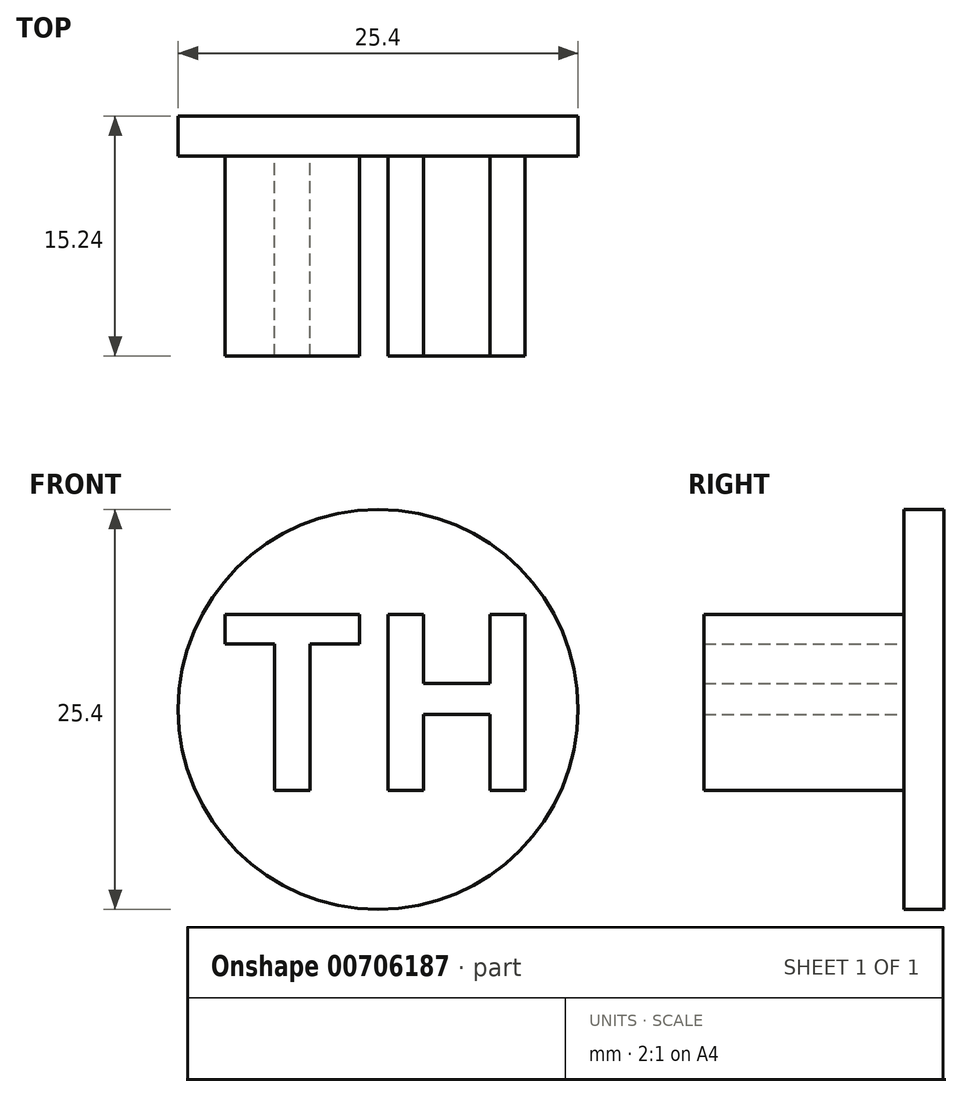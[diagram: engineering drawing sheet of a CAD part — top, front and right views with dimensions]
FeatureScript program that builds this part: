
annotation { "Feature Type Name" : "Feature", "Feature Type Description" : "" }
export const myFeature = defineFeature(function(context is Context, id is Id, definition is map)
    precondition{}
    {
        {
            var Q0;
            Q0=qCreatedBy(makeId("Front.planeOp"),FACE);
            var sketch = newSketch(context, id + "F0", { "sketchPlane" : qUnion([Q0])});
            skCircle(sketch, "E0", {"center": v(0, 0) * mm, "radius": 12.7 * mm});
            skSolve(sketch);
        }
        {
            var Q0;
            Q0=makeQuery(id+"F0.imprint","IMPRINT",FACE,{"disambiguationData":[TD([[makeQuery(id+"F0.imprint","IMPRINT",EDGE,{"derivedFrom":sQuery(id+"F0.wireOp",EDGE,"E0")}),1.0]])]});
            extrude(context, id + "F1", {"entities" : qUnion([Q0]), "depth" : 2.54 * mm, "offsetDistance" : 25.4 * mm});
        }
        {
            var Q0;
            Q0=makeQuery(id+"F1.opExtrude","CAP_FACE",FACE,{"disambiguationData":[OSD([sQuery(id+"F0.wireOp",EDGE,"E0")])],"isStart":false});
            var sketch = newSketch(context, id + "F2", { "sketchPlane" : qUnion([Q0])});
            skText(sketch, "E1", { "text": "TH ", "fontName": "NotoSansCJKtc-Bold.otf"});
            const initialGuessF2  = {"E1": [-0.01016, -0.00513, 1, 0, 0.01086]};
            skSetInitialGuess(sketch, initialGuessF2);
            skSolve(sketch);
        }
        {
            var Q0;
            Q0=makeQuery(id+"F2.imprint","IMPRINT",FACE,{"disambiguationData":[TD([[makeQuery(id+"F2.imprint","IMPRINT",EDGE,{"derivedFrom":sQuery(id+"F2.wireOp",EDGE,"E1.sketch_text.stroke-0")}),1.0]])]});
            var Q1;
            Q1=makeQuery(id+"F2.imprint","IMPRINT",FACE,{"disambiguationData":[TD([[makeQuery(id+"F2.imprint","IMPRINT",EDGE,{"derivedFrom":sQuery(id+"F2.wireOp",EDGE,"E1.sketch_text.stroke-8")}),1.0]])]});
            extrude(context, id + "F3", {"entities" : qUnion([Q0, Q1]), "operationType" : NewBodyOperationType.ADD, "depth" : 12.7 * mm, "offsetDistance" : 25.4 * mm});
        }
    });
